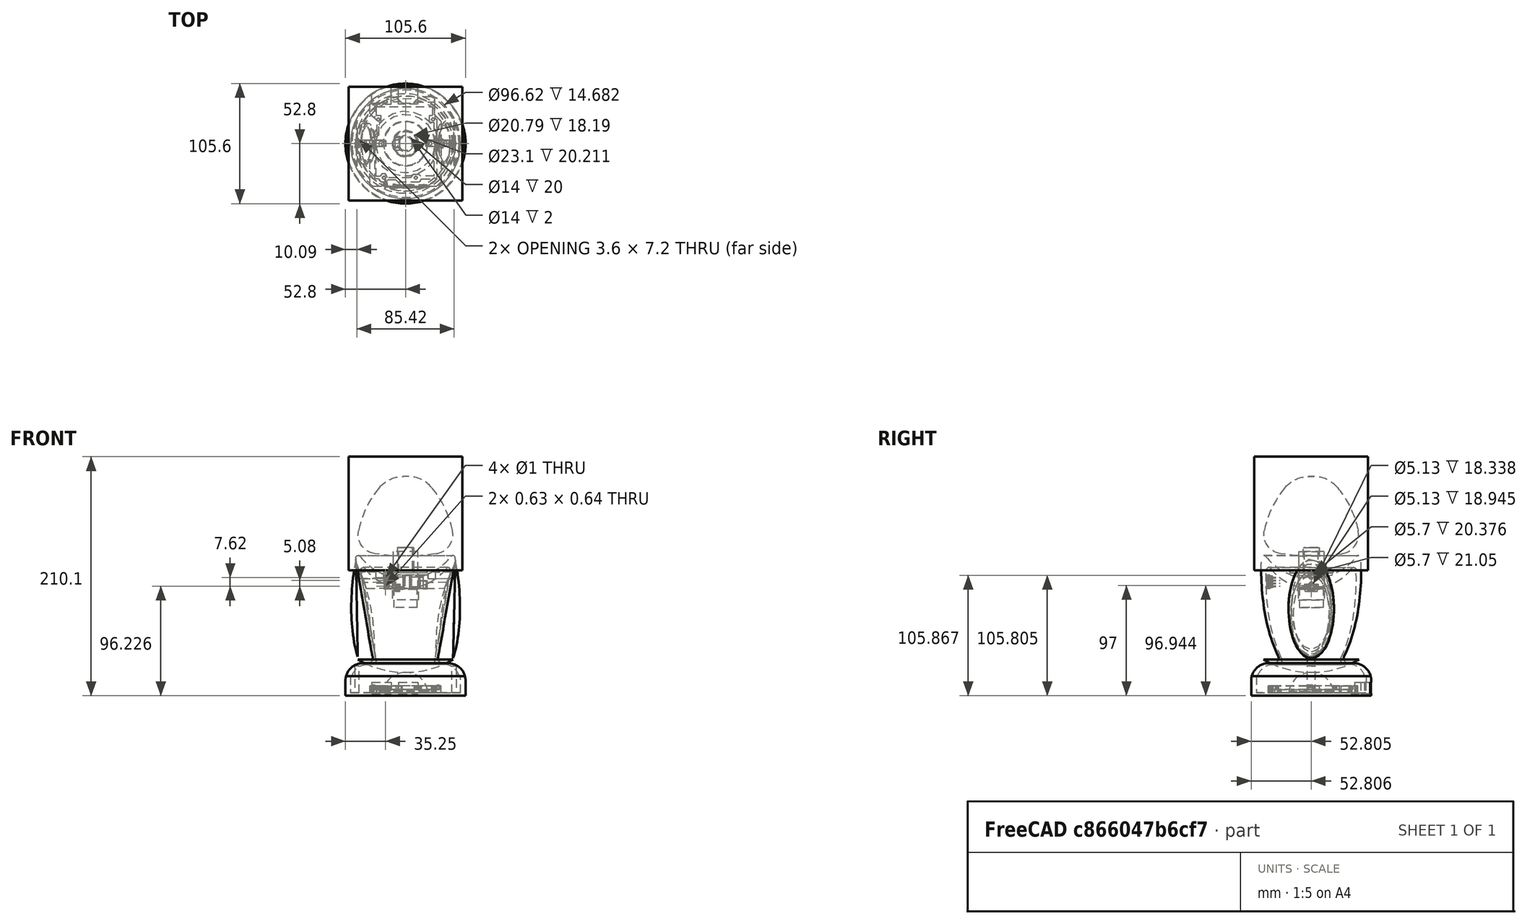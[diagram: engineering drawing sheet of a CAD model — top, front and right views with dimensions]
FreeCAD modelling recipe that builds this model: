
FCSTD DOCUMENT  (FreeCAD 0.20R29410 (Git))
Label: evaV1
License: All rights reserved
LicenseURL: https://en.wikipedia.org/wiki/All_rights_reserved
objects: Part::FeaturePython×33, Part::Cut×16, App::DocumentObjectGroup×11, Part::Part2DObjectPython×11, Part::Feature×9, Part::MultiFuse×9, Part::Extrusion×8, Part::Box×8, Raytracing::LuxFeature×8, Part::Sphere×4, Part::Cylinder×4, Part::Fillet×3, App::FeaturePython×3, Mesh::Feature×2, Sketcher::SketchObject×1, Part::Revolution×1, Part::Refine×1, Raytracing::LuxProject×1
note: 108 computed .brp shape members not serialized (recipe doc carries the construction recipe); baked Part::Feature solids carry a one-line shape summary decoded from their .brp

FEATURE [Part::Sphere] Sphere
  Angle1 = -90
  Angle2 = 10
  Angle3 = 360
  AttacherType = Attacher::AttachEngine3D
  Placement = pos=(0,0,0.478785) rot=(0,0,1;0rad)
  Radius = 20
FEATURE [Part::FeaturePython] Clone  label="Sphere001"  # Draft clone (typed FeaturePython)
  AttacherType = Attacher::AttachEngine3D
  Fuse = false
  Objects = -> [Sphere]
  Placement = pos=(0,0,-4.51485) rot=(0,0,1;0rad)
  Scale = (1,1,2.3)
FEATURE [Part::Sphere] Sphere001  label="Sphere002"
  Angle1 = -90
  Angle2 = 90
  Angle3 = 360
  AttacherType = Attacher::AttachEngine3D
  Placement = pos=(0,0,14.8901) rot=(0,0,1;0rad)
  Radius = 23
FEATURE [Part::Cut] Cut  label="Body"
  Base = -> Clone
  Tool = -> Sphere001
FEATURE [Part::Fillet] Fillet  label="EvaBody"
  Base = -> Cut
  Edges = 1 edges r=1: [Edge1]
  Placement = pos=(0,0,54.9218) rot=(0,0,1;0rad)
FEATURE [Part::Sphere] Sphere003  label="Sphere004"
  Angle1 = -90
  Angle2 = -60
  Angle3 = 360
  AttacherType = Attacher::AttachEngine3D
  Placement = pos=(-0.0204827,0,65.9269) rot=(0,0,1;0rad)
  Radius = 39.5
FEATURE [Part::FeaturePython] Clone002  label="Sphere005"  # Draft clone (typed FeaturePython)
  AttacherType = Attacher::AttachEngine3D
  Fuse = false
  Objects = -> [Sphere003]
  Placement = pos=(-0.0204827,1e-15,104.24) rot=(0,0,1;0rad)
  Scale = (2.12,2.12,2.12)
FEATURE [Part::Sphere] Sphere002  label="UpperHead"
  Angle1 = 10
  Angle2 = 90
  Angle3 = 360
  AttacherType = Attacher::AttachEngine3D
  Placement = pos=(0,0,0.478785) rot=(0,0,1;0rad)
  Radius = 20
FEATURE [App::DocumentObjectGroup] Group  label="Build"
  Group = -> [Sphere003,Clone002,Sphere002]
FEATURE [Sketcher::SketchObject] Sketch  label="HeadSketch"
  FullyConstrained = false
  MapMode = 2
  Placement = pos=(0,0,54.9218) rot=(0,0,1;0rad)
  Support = -> [Fillet]
  sketch-geometry (24):
    g0: LineSegment StartX=-21.7965 StartY=-11.3382 StartZ=0 EndX=21.2048 EndY=-12.4097 EndZ=0
    g1: Circle CenterX=0 CenterY=0 CenterZ=0 NormalX=0 NormalY=0 NormalZ=1 AngleXU=0 Radius=24.5691
    g2: LineSegment StartX=21.3552 StartY=0 StartZ=0 EndX=13.3962 EndY=-0.101077 EndZ=0
    g3: LineSegment StartX=-13.3802 StartY=-0.143385 StartZ=0 EndX=-19.9121 EndY=0 EndZ=0
    g4: LineSegment StartX=-3.37523e-05 StartY=-11.8813 StartZ=0 EndX=0 EndY=-22.0143 EndZ=0
    g5: LineSegment StartX=13.3962 StartY=-0.101077 StartZ=0 EndX=-3.37523e-05 EndY=-11.8813 EndZ=0
    g6: LineSegment StartX=-13.3802 StartY=-0.143385 StartZ=0 EndX=-3.37523e-05 EndY=-11.8813 EndZ=0
    g7: LineSegment StartX=0 StartY=17.1433 StartZ=0 EndX=0.581079 EndY=17.1433 EndZ=0
    g8: LineSegment StartX=20.5247 StartY=13.5047 StartZ=0 EndX=23.5963 EndY=12.9178 EndZ=0
    g9: GeomPoint X=0 Y=-1.93536 Z=0
    g10: LineSegment StartX=7.19648 StartY=-0.989266 StartZ=0 EndX=0 EndY=-1.93536 EndZ=0
    g11: LineSegment StartX=0 StartY=-1.93536 StartZ=0 EndX=-7.03873 EndY=-0.87588 EndZ=0
    g12: LineSegment StartX=0 StartY=17.1433 StartZ=0 EndX=0 EndY=0 EndZ=0
    g13: ArcOfCircle CenterX=0.581079 CenterY=9.86833 CenterZ=0 NormalX=0 NormalY=0 NormalZ=1 AngleXU=0 Radius=7.27493 StartAngle=0.693262 EndAngle=1.5708
    g14: ArcOfCircle CenterX=-0.581079 CenterY=9.88205 CenterZ=0 NormalX=0 NormalY=0 NormalZ=1 AngleXU=0 Radius=7.26121 StartAngle=1.5708 EndAngle=2.33078
    g15: LineSegment StartX=6.74134 StartY=12.7057 StartZ=0 EndX=0.581079 EndY=17.1433 EndZ=0
    g16: LineSegment StartX=-6.7178 StartY=12.6732 StartZ=0 EndX=-0.581079 EndY=17.1433 EndZ=0
    g17: ArcOfCircle CenterX=6.60715 CenterY=3.49348 CenterZ=0 NormalX=0 NormalY=0 NormalZ=1 AngleXU=0 Radius=4.52132 StartAngle=4.84311 EndAngle=6.48567
    g18: ArcOfCircle CenterX=-6.35756 CenterY=3.64951 CenterZ=0 NormalX=0 NormalY=0 NormalZ=1 AngleXU=0 Radius=4.57636 StartAngle=3.05715 EndAngle=4.56299
    g19: LineSegment StartX=10.3085 StartY=5.26228 StartZ=0 EndX=7.19648 EndY=-0.989266 EndZ=0
    g20: LineSegment StartX=-7.03873 StartY=-0.87588 StartZ=0 EndX=-10.097 EndY=5.40212 EndZ=0
    g21: ArcOfCircle CenterX=-11.5876 CenterY=-0.241793 CenterZ=0 NormalX=0 NormalY=0 NormalZ=1 AngleXU=0 Radius=23.0955 StartAngle=0.202481 EndAngle=0.693262
    g22: ArcOfCircle CenterX=6.36602 CenterY=2.57249 CenterZ=0 NormalX=0 NormalY=0 NormalZ=1 AngleXU=0 Radius=17.3454 StartAngle=2.33078 EndAngle=3.05715
    g23: LineSegment StartX=0 StartY=-1.93536 StartZ=0 EndX=0 EndY=17.1433 EndZ=0
  constraints (30):
    c: PointOnObject(g0,g1)
    c: PointOnObject(g0,g1)
    c: Coincident(g1,g-1)
    c: PointOnObject(g2,g-1)
    c: PointOnObject(g4,g0)
    c: Coincident(g5,g2)
    c: Coincident(g5,g4)
    c: Coincident(g6,g3)
    c: Coincident(g6,g5)
    c: Horizontal(g7)
    c: PointOnObject(g8,g1)
    c: PointOnObject(g9,g-2)
    c: Coincident(g10,g9)
    c: Coincident(g11,g10)
    c: Coincident(g12,g1)
    c: Tangent(g7,g13) = 1.5708
    c: Coincident(g15,g7)
    c: Equal(g15,g16)
    c: Vertical(g12)
    c: Tangent(g10,g17) = 1.5708
    c: Tangent(g11,g18) = 1.5708
    c: Coincident(g19,g10)
    c: Coincident(g20,g11)
    c: Equal(g19,g20)
    c: Tangent(g17,g21) = -1.5708
    c: Tangent(g13,g21) = -1.5708
    c: Tangent(g14,g22) = -1.5708
    c: Tangent(g18,g22) = -1.5708
    c: Coincident(g23,g10)
    c: PointOnObject(g7,g12)
FEATURE [Part::Feature] Sketch001
  shape: bbox 11.13 x 19.08 x 2e-07 mm, 0 faces, 0 solids (baked)
FEATURE [Part::Revolution] Revolve
  Angle = 360
  Axis = (0,1,0)
  Base = (0,0,0)
  FaceMakerClass = Part::FaceMakerBullseye
  Placement = pos=(0,-1.30463,1.78342) rot=(1,0,0;1.5708rad)
  Solid = false
  Source = -> Sketch001
  Symmetric = false
FEATURE [Part::FeaturePython] Clone003  label="Head"  # Draft clone (typed FeaturePython)
  AttacherType = Attacher::AttachEngine3D
  Fuse = false
  Objects = -> [Revolve]
  Placement = pos=(0,2.70425e-10,58.4524) rot=(1,0,0;1.5708rad)
  Scale = (1.7,1.7,1.7)
FEATURE [Part::Cylinder] Cylinder  label="Neck"
  Angle = 360
  AttacherType = Attacher::AttachEngine3D
  FirstAngle = 0
  Height = 15
  Placement = pos=(0,0,42.6404) rot=(0,0,1;0rad)
  Radius = 5
  SecondAngle = 0
FEATURE [Part::Cylinder] Cylinder001  label="Base"
  Angle = 360
  AttacherType = Attacher::AttachEngine3D
  FirstAngle = 0
  Height = 13
  Radius = 24
  SecondAngle = 0
FEATURE [App::DocumentObjectGroup] Group002  label="Drafts"
  Group = -> [Sphere,Group,Sketch,Revolve]
FEATURE [Part::Part2DObjectPython] Rectangle  label="ArmCut"  # Draft 2D object (typed FeaturePython)
  Area = 5447.74
  ChamferSize = 0
  Columns = 1
  FilletRadius = 0
  Height = 81.8196
  Length = 66.5823
  MakeFace = true
  Placement = pos=(-12.9997,-33.2912,14.176) rot=(0.541699,0.541699,0.642747;1.99907rad)
  Rows = 1
FEATURE [Part::Part2DObjectPython] Clone2D  label="ArmCutLeft"  # Draft 2D object (typed FeaturePython)
  Fuse = false
  Objects = -> [Rectangle]
  Placement = pos=(12.8819,-33.2912,14.5327) rot=(0.608338,0.608338,0.509755;2.19875rad)
  Scale = (1,1,1)
FEATURE [Part::FeaturePython] Slice  # WARN: FeaturePython — macro-defined, semantics opaque (R4)
  Base = -> Fillet
  Mode = 1
  Tolerance = 0
  Tools = -> [Clone2D,Rectangle]
FEATURE [Part::FeaturePython] Slice_child0  label="Slice.0"  # WARN: FeaturePython — macro-defined, semantics opaque (R4)
  Base = -> Slice
  FilterType = 1
  Invert = false
  OverrideMaxVal = 0
  WindowFrom = 80
  WindowTo = 100
  items = 0
FEATURE [Part::FeaturePython] Slice_child1  label="RightArm"  # WARN: FeaturePython — macro-defined, semantics opaque (R4)
  Base = -> Slice
  FilterType = 1
  Invert = false
  OverrideMaxVal = 0
  Placement = pos=(8.47277,0,-2.40038) rot=(0,-1,0;0.152637rad)
  WindowFrom = 80
  WindowTo = 100
  items = 1
FEATURE [Part::FeaturePython] Slice_child2  label="LeftArm"  # WARN: FeaturePython — macro-defined, semantics opaque (R4)
  Base = -> Slice
  FilterType = 1
  Invert = false
  OverrideMaxVal = 0
  Placement = pos=(-8.37005,0,-2.38162) rot=(0,1,0;0.152455rad)
  WindowFrom = 80
  WindowTo = 100
  items = 2
FEATURE [Part::FeaturePython] Clone004  label="Slice.003"  # Draft clone (typed FeaturePython)
  AttacherType = Attacher::AttachEngine3D
  Fuse = false
  Objects = -> [Slice_child2]
  Placement = pos=(-33.7337,0,70.5771) rot=(0,1,0;3.14159rad)
  Scale = (1,1,1)
FEATURE [Part::FeaturePython] Clone005  label="Slice.004"  # Draft clone (typed FeaturePython)
  AttacherType = Attacher::AttachEngine3D
  Fuse = false
  Objects = -> [Slice_child1]
  Placement = pos=(33.43,0,69.7879) rot=(0,1,0;3.14159rad)
  Scale = (1,1,1)
FEATURE [Part::Cut] Cut001
  Base = -> Slice_child0
  Tool = -> Clone004
FEATURE [Part::Cut] Cut002  label="CuttedBody"
  Base = -> Cut001
  Tool = -> Clone005
FEATURE [Part::Part2DObjectPython] Circle  # Draft 2D object (typed FeaturePython)
  Area = 4.35646
  FirstAngle = 0
  LastAngle = 0
  MakeFace = true
  Placement = pos=(-19.6772,0.00266592,48.0107) rot=(0,1,0;1.55304rad)
  Radius = 1.17758
FEATURE [Part::Extrusion] Extrude002  label="RightArm Support"
  Base = -> Circle
  Dir = (0.999842,2e-15,0.0177575)
  DirMode = 2
  FaceMakerClass = Part::FaceMakerBullseye
  LengthFwd = 8
  LengthRev = 0
  Placement = pos=(31.7394,1.9e-15,0) rot=(0,0,1;0rad)
  Solid = false
  Symmetric = false
FEATURE [Part::FeaturePython] Clone006  label="LeftArm Support001"  # Draft clone (typed FeaturePython)
  AttacherType = Attacher::AttachEngine3D
  Fuse = false
  Objects = -> [Extrude002]
  Placement = pos=(-0.14219,0,0) rot=(0,0,1;0rad)
  Scale = (1,1,1)
FEATURE [Part::Part2DObjectPython] Clone2D001  label="Circle (2D)"  # Draft 2D object (typed FeaturePython)
  Fuse = false
  Objects = -> [Circle]
  Placement = pos=(-19.6772,0.00266592,48.0107) rot=(0,1,0;1.55304rad)
  Scale = (1.1,1.1,1.1)
FEATURE [Part::Extrusion] Extrude003  label="ExtrusionHoleLeft"
  Base = -> Clone2D001
  Dir = (0.999842,2e-15,0.0177575)
  DirMode = 2
  FaceMakerClass = Part::FaceMakerBullseye
  LengthFwd = 11
  LengthRev = 0
  Placement = pos=(28.742,1.8e-15,0) rot=(0,0,1;0rad)
  Solid = false
  Symmetric = false
FEATURE [Part::FeaturePython] Clone007  label="ExtrusionHoleRight"  # Draft clone (typed FeaturePython)
  AttacherType = Attacher::AttachEngine3D
  Fuse = false
  Objects = -> [Extrude003]
  Scale = (1,1,1)
FEATURE [Part::Cut] Cut003
  Base = -> Cut002
  Tool = -> Extrude003
FEATURE [Part::Cut] Cut004  label="BodyWithArmHoles"
  Base = -> Cut003
  Tool = -> Clone007
FEATURE [Part::MultiFuse] Fusion  label="RightArmWithSupport"
  Shapes = -> [Slice_child1,Extrude002]
FEATURE [Part::Part2DObjectPython] Circle001  # Draft 2D object (typed FeaturePython)
  Area = 237.663
  FirstAngle = 0
  LastAngle = 0
  MakeFace = true
  Placement = pos=(1e-15,0,57.6404) rot=(0,0,1;0rad)
  Radius = 8.69772
FEATURE [Part::Extrusion] Extrude  label="NeckBlock"
  Base = -> Circle001
  Dir = (0,0,1)
  DirMode = 2
  FaceMakerClass = Part::FaceMakerBullseye
  LengthFwd = 1
  LengthRev = 0
  Placement = pos=(0,0,-8.59498) rot=(0,0,1;0rad)
  Solid = false
  Symmetric = false
FEATURE [Part::MultiFuse] Fusion001  label="LeftArmWithSupport"
  Shapes = -> [Slice_child2,Clone006]
FEATURE [Part::FeaturePython] Clone009  label="ExpandedNeck"  # Draft clone (typed FeaturePython)
  AttacherType = Attacher::AttachEngine3D
  Fuse = false
  Objects = -> [Cylinder]
  Placement = pos=(0,0,38.2322) rot=(0,0,1;0rad)
  Scale = (1.05,1.05,1.05)
FEATURE [Part::Cut] Cut005  label="BodyWithNeckHole"
  Base = -> Cut004
  Tool = -> Clone009
FEATURE [Part::MultiFuse] Fusion002  label="NeckWithBlock"
  Shapes = -> [Cylinder,Extrude]
FEATURE [Part::FeaturePython] Clone010  label="ExpandedNeck001"  # Draft clone (typed FeaturePython)
  AttacherType = Attacher::AttachEngine3D
  Fuse = false
  Objects = -> [Clone009]
  Placement = pos=(0,0,51.4204) rot=(0,0,1;0rad)
  Scale = (1,1,1)
FEATURE [Part::Cut] Cut006  label="HeadWithNeckHole"
  Base = -> Clone003
  Tool = -> Clone010
FEATURE [Part::MultiFuse] Fusion003  label="BodyWithBase"
  Shapes = -> [Cylinder001,Cut005]
FEATURE [Part::Fillet] Fillet001  label="RoundedBodyBase"
  Base = -> Fusion003
  Edges = 1 edges r=2: [Edge4]
FEATURE [Part::Fillet] Fillet002  label="RoundedBodyWithBase"
  Base = -> Fillet001
  Edges = 1 edges r=7: [Edge4]
FEATURE [App::DocumentObjectGroup] GrExplode_Slice  label="Non-Sized-Parts"
  Group = -> [Fusion,Fusion001,Fusion002,Cut006,Fillet002]
FEATURE [App::DocumentObjectGroup] Group003  label="Build001"
  Group = -> [Fusion003]
FEATURE [Mesh::Feature] Alhambra_II_Support_NO_text  label="Alhambra-II-Support-NO-text"
FEATURE [Part::Feature] Alhambra_II_Support_NO_text001
  shape: bbox 78.88 x 62.84 x 6.975 mm, 1078 faces, 0 solids (baked)
FEATURE [Part::Refine] Alhambra_II_Support_NO_text001001  label="RefinedFPGASupport"
  Placement = pos=(2.6e-14,86.6242,2.50937) rot=(0,0,-1;1.5708rad)
  Source = -> Alhambra_II_Support_NO_text001
FEATURE [Part::FeaturePython] Clone011  label="RightArmWithSupport001"  # Draft clone (typed FeaturePython)
  AttacherType = Attacher::AttachEngine3D
  Fuse = false
  Objects = -> [Fusion]
  Scale = (2.2,2.2,2.2)
FEATURE [Part::FeaturePython] Clone012  label="LeftArmWithSupport001"  # Draft clone (typed FeaturePython)
  AttacherType = Attacher::AttachEngine3D
  Fuse = false
  Objects = -> [Fusion001]
  Scale = (2.2,2.2,2.2)
FEATURE [Part::FeaturePython] Clone013  label="NeckWithBlock001"  # Draft clone (typed FeaturePython)
  AttacherType = Attacher::AttachEngine3D
  Fuse = false
  Objects = -> [Fusion002]
  Scale = (2.2,2.2,2.2)
FEATURE [Part::FeaturePython] Clone014  label="HeadWithNeckHole001"  # Draft clone (typed FeaturePython)
  AttacherType = Attacher::AttachEngine3D
  Fuse = false
  Objects = -> [Cut006]
  Scale = (2.2,2.2,2.2)
FEATURE [Part::FeaturePython] Clone015  label="RoundedBodyWithBase001"  # Draft clone (typed FeaturePython)
  AttacherType = Attacher::AttachEngine3D
  Fuse = false
  Objects = -> [Fillet002]
  Scale = (2.2,2.2,2.2)
FEATURE [App::DocumentObjectGroup] Group005  label="Resized Parts"
  Group = -> [Clone011,Clone012,Clone013,Clone014,Clone015]
FEATURE [Part::Part2DObjectPython] Rectangle001  label="BaseSlicer"  # Draft 2D object (typed FeaturePython)
  Area = 17833.6
  ChamferSize = 0
  Columns = 1
  FilletRadius = 0
  Height = 133.871
  Length = 133.215
  MakeFace = true
  Placement = pos=(-69.7967,-69.2809,17.1918) rot=(0,0,1;0rad)
  Rows = 1
FEATURE [Part::FeaturePython] Slice001  label="BodySlice"  # WARN: FeaturePython — macro-defined, semantics opaque (R4)
  Base = -> Clone015
  Mode = 1
  Tolerance = 0
  Tools = -> [Rectangle001]
FEATURE [Part::FeaturePython] Slice001_child0  label="EvaBody001"  # WARN: FeaturePython — macro-defined, semantics opaque (R4)
  Base = -> Slice001
  FilterType = 1
  Invert = false
  OverrideMaxVal = 0
  WindowFrom = 80
  WindowTo = 100
  items = 0
FEATURE [Part::FeaturePython] Slice001_child1  label="FPGABase"  # WARN: FeaturePython — macro-defined, semantics opaque (R4)
  Base = -> Slice001
  FilterType = 1
  Invert = false
  OverrideMaxVal = 0
  WindowFrom = 80
  WindowTo = 100
  items = 1
FEATURE [Part::Part2DObjectPython] Circle002  # Draft 2D object (typed FeaturePython)
  Area = 7332.14
  FirstAngle = 0
  LastAngle = 0
  MakeFace = true
  Placement = pos=(-7.1e-15,-3.9e-15,17.1918) rot=(0,0,1;0rad)
  Radius = 48.3104
FEATURE [Part::Extrusion] Extrude005
  Base = -> Circle002
  Dir = (0,0,1)
  DirMode = 2
  FaceMakerClass = Part::FaceMakerBullseye
  LengthFwd = 15
  LengthRev = 0
  Placement = pos=(0,0,-14.6824) rot=(0,0,1;0rad)
  Solid = false
  Symmetric = false
FEATURE [Part::Cut] Cut007  label="HollowFPGABase"
  Base = -> Slice001_child1
  Tool = -> Extrude005
FEATURE [Part::Box] Box  label="Cubo"
  AttacherType = Attacher::AttachEngine3D
  Height = 10
  Length = 17
  Placement = pos=(-6.05737,34.8465,1.87069) rot=(0,0,1;0rad)
  Width = 30
FEATURE [Part::Cut] Cut008  label="FPGABaseWConnectionHole1"
  Base = -> Cut007
  Tool = -> Box
FEATURE [Part::FeaturePython] Clone016  label="Cubo001"  # Draft clone (typed FeaturePython)
  AttacherType = Attacher::AttachEngine3D
  Fuse = false
  Objects = -> [Box]
  Placement = pos=(-29.6318,34.8465,1.87069) rot=(0,0,1;0rad)
  Scale = (1,1,1)
FEATURE [Part::Cut] Cut009  label="FPGABaseWithHoles"
  Base = -> Cut008
  Tool = -> Clone016
FEATURE [Part::FeaturePython] Clone018  label="EvaBodyHollow001"  # WARN: FeaturePython — macro-defined, semantics opaque (R4)
  AttacherType = Attacher::AttachEngine3D
  Fuse = false
  Placement = pos=(-1e-15,0,1.71918) rot=(0,0,1;0rad)
  Scale = (0.9,0.9,0.9)
FEATURE [Part::Feature] Shell_solid  label="EvaBodyHollow"
  shape: bbox 204.6 x 181.6 x 135.9 mm, 34 faces (baked)
FEATURE [Part::Cylinder] Cylinder002  label="LeftBridge"
  Angle = 180
  AttacherType = Attacher::AttachEngine3D
  FirstAngle = 0
  Height = 26
  Placement = pos=(-40.91,0,0) rot=(0,0,1;1.5708rad)
  Radius = 3.6
  SecondAngle = 0
FEATURE [Part::Cylinder] Cylinder003  label="RightBridge"
  Angle = 180
  AttacherType = Attacher::AttachEngine3D
  FirstAngle = 0
  Height = 26
  Placement = pos=(40.91,0,0) rot=(0,0,-1;1.5708rad)
  Radius = 3.6
  SecondAngle = 0
FEATURE [Part::FeaturePython] Clone019  label="LeftBridge001"  # Draft clone (typed FeaturePython)
  AttacherType = Attacher::AttachEngine3D
  Fuse = false
  Objects = -> [Cylinder002]
  Placement = pos=(-40.91,0,0) rot=(0,0,1;1.5708rad)
  Scale = (1,1,1)
FEATURE [Part::FeaturePython] Clone020  label="RightBridge001"  # Draft clone (typed FeaturePython)
  AttacherType = Attacher::AttachEngine3D
  Fuse = false
  Objects = -> [Cylinder003]
  Placement = pos=(40.91,0,0) rot=(0,0,-1;1.5708rad)
  Scale = (1,1,1)
FEATURE [Part::Cut] Cut010  label="EvaConnectableLeft"
  Base = -> Shell_solid
  Tool = -> Clone019
FEATURE [Part::Cut] Cut011  label="EvaBodyConnectable"
  Base = -> Cut010
  Tool = -> Clone020
FEATURE [Part::MultiFuse] Fusion004  label="BaseFPGAWithBridges"
  Shapes = -> [Cylinder003,Cylinder002,Cut009]
FEATURE [Mesh::Feature] Servo_SG90  label="Servo-SG90"
FEATURE [App::DocumentObjectGroup] Group004  label="External"
  Group = -> [Alhambra_II_Support_NO_text001001,Servo_SG90,Alhambra_II_Support_NO_text001,Alhambra_II_Support_NO_text]
FEATURE [Part::Feature] Servo_SG90001  label="RefinedServo"
  Placement = pos=(16.3519,-0.186281,64.3614) rot=(0,0,1;1.5708rad)
  shape: bbox 32.4 x 11.8 x 29.9 mm, 2326 faces, 0 solids (baked)
FEATURE [App::FeaturePython] Dimension  # Draft dimension (typed FeaturePython)
  Diameter = false
  Dimline = (-23.6882,-74.8393,0)
  Direction = (0,0,0)
  Distance = 105.6
  End = (52.8,-1.32e-14,0)
  Normal = (0,0,-1)
  Start = (-52.8,2.99e-14,0)
FEATURE [App::FeaturePython] Dimension001  # Draft dimension (typed FeaturePython)
  Diameter = false
  Dimline = (-91.8745,5.94944e-10,192.711)
  Direction = (0,0,0)
  Distance = 192.711
  End = (0,5.94949e-10,192.711)
  Normal = (0,0,1)
  Start = (-1.8e-15,-2.1e-15,0)
FEATURE [App::FeaturePython] Dimension002  # Draft dimension (typed FeaturePython)
  Diameter = false
  Dimline = (-43.7741,108.073,121.137)
  Direction = (0,0,0)
  Distance = 87.5482
  End = (-43.7741,205.609,121.137)
  Normal = (0,0,1)
  Start = (43.7741,205.609,121.137)
FEATURE [Part::Feature] Feature  label="OLED_0.91_128x034"
  Placement = pos=(0,-36.5535,100.036) rot=(1,0,0;1.5708rad)
  shape: bbox 38.3 x 11.46 x 12.1 mm, 1137 faces, 52 solids (baked)
FEATURE [Part::Feature] Alhambra_II_Support_NO_text001001_solid  label="RefinedFPGASupport (Solid)"
  shape: bbox 62.84 x 78.88 x 6.975 mm, 342 faces (baked)
FEATURE [Part::MultiFuse] Fusion005  label="BaseFPGA"
  Shapes = -> [Alhambra_II_Support_NO_text001001_solid,Fusion004]
FEATURE [App::DocumentObjectGroup] Group008  label="Measurements"
  Group = -> [Dimension,Dimension001,Dimension002]
FEATURE [Part::FeaturePython] Clone021  label="RightArmWithSupport002"  # Draft clone (typed FeaturePython)
  AttacherType = Attacher::AttachEngine3D
  Fuse = false
  Objects = -> [Clone011]
  Scale = (1,1,1)
FEATURE [Part::FeaturePython] Clone022  label="LeftArmWithSupport002"  # Draft clone (typed FeaturePython)
  AttacherType = Attacher::AttachEngine3D
  Fuse = false
  Objects = -> [Clone012]
  Scale = (1,1,1)
FEATURE [Part::FeaturePython] Clone023  label="NeckWithBlock002"  # Draft clone (typed FeaturePython)
  AttacherType = Attacher::AttachEngine3D
  Fuse = false
  Objects = -> [Clone013]
  Scale = (1,1,1)
FEATURE [Part::Feature] Clone023_solid  label="NeckWithBlock002 (Solid)"
  shape: bbox 38.27 x 38.27 x 33 mm, 7 faces (baked)
FEATURE [Part::FeaturePython] Clone024  label="HeadWithNeckHole002"  # Draft clone (typed FeaturePython)
  AttacherType = Attacher::AttachEngine3D
  Fuse = false
  Objects = -> [Clone014]
  Scale = (1,1,1)
FEATURE [Part::Box] Box001  label="BridgeHole1"
  AttacherType = Attacher::AttachEngine3D
  Height = 5.3
  Length = 5
  Placement = pos=(-9.5,-6,92.81) rot=(0,0,1;0rad)
  Width = 3
FEATURE [Part::Box] Box002  label="Cubo003"
  AttacherType = Attacher::AttachEngine3D
  Height = 1
  Length = 4
  Placement = pos=(0,1,0) rot=(0,0,1;0rad)
  Width = 7
FEATURE [Part::Box] Box003  label="Cubo004"
  AttacherType = Attacher::AttachEngine3D
  Height = 5.3
  Length = 4
  Placement = pos=(0,-1,0) rot=(0,0,1;0rad)
  Width = 2
FEATURE [Part::Box] Box006  label="Cubo005"
  AttacherType = Attacher::AttachEngine3D
  Height = 100
  Length = 100
  Placement = pos=(-50,-50,110.1) rot=(0,0,1;0rad)
  Width = 100
FEATURE [Part::Box] Box007  label="Cubo006"
  AttacherType = Attacher::AttachEngine3D
  Height = 5.3
  Length = 4
  Placement = pos=(0,8,0) rot=(0,0,1;0rad)
  Width = 2
FEATURE [Part::Box] Box008  label="BridgeHole2"
  AttacherType = Attacher::AttachEngine3D
  Height = 5.3
  Length = 5
  Placement = pos=(-9.5,3,92.81) rot=(0,0,1;0rad)
  Width = 3
FEATURE [Part::MultiFuse] Fusion007  label="Bridge"
  Placement = pos=(-9,-4.5,91.81) rot=(0,0,1;0rad)
  Shapes = -> [Box003,Box002,Box007]
FEATURE [Part::Feature] Solid001
  shape: bbox 22 x 22 x 1.001 mm, 13 faces (baked)
FEATURE [App::DocumentObjectGroup] Group009  label="Tests"
  Group = -> [Solid001,Box006]
FEATURE [Part::Feature] Solid  label="Head001"
  shape: bbox 90.1 x 90.1 x 69.84 mm, 6 faces (baked)
FEATURE [Part::MultiFuse] Fusion008  label="HeadWithNeck"
  Shapes = -> [Clone023_solid,Solid]
FEATURE [App::DocumentObjectGroup] Group006  label="Building"
  Group = -> [Slice001_child0,Clone018,Clone024,Clone023,Fusion008]
FEATURE [Part::FeaturePython] Clone025  label="HeadWithNeck001"  # Draft clone (typed FeaturePython)
  AttacherType = Attacher::AttachEngine3D
  Fuse = false
  Objects = -> [Fusion008]
  Scale = (1,1,1)
FEATURE [Part::Box] Box009  label="Cubo007"
  AttacherType = Attacher::AttachEngine3D
  Height = 100
  Length = 100
  Placement = pos=(-50,-50,110.1) rot=(0,0,1;0rad)
  Width = 100
FEATURE [Part::FeaturePython] Slice002  # WARN: FeaturePython — macro-defined, semantics opaque (R4)
  Base = -> Clone025
  Mode = 1
  Tolerance = 0
  Tools = -> [Box009]
FEATURE [Part::FeaturePython] Slice002_child0  label="LowerHead001"  # WARN: FeaturePython — macro-defined, semantics opaque (R4)
  Base = -> Slice002
  FilterType = 1
  Invert = false
  OverrideMaxVal = 0
  WindowFrom = 80
  WindowTo = 100
  items = 0
FEATURE [Part::FeaturePython] Slice002_child1  label="LowerHead"  # WARN: FeaturePython — macro-defined, semantics opaque (R4)
  Base = -> Slice002
  FilterType = 1
  Invert = false
  OverrideMaxVal = 0
  WindowFrom = 80
  WindowTo = 100
  items = 1
FEATURE [Part::Part2DObjectPython] Circle003  # Draft 2D object (typed FeaturePython)
  Area = 153.938
  FirstAngle = 0
  LastAngle = 0
  MakeFace = true
  Placement = pos=(-2e-15,0,110.1) rot=(0.707107,-0.707107,0;3.14159rad)
  Radius = 7
FEATURE [Part::Part2DObjectPython] Circle004  # Draft 2D object (typed FeaturePython)
  Area = 113.097
  FirstAngle = 0
  LastAngle = 0
  MakeFace = true
  Placement = pos=(-2e-15,0,110.1) rot=(0.707107,-0.707107,0;3.14159rad)
  Radius = 6
FEATURE [Part::Extrusion] Extrude006
  Base = -> Circle003
  Dir = (0,0,-1)
  DirMode = 2
  FaceMakerClass = Part::FaceMakerBullseye
  LengthFwd = -20
  LengthRev = 0
  Solid = false
  Symmetric = false
FEATURE [Part::Cut] Cut012  label="UpperHeadWithHole"
  Base = -> Slice002_child1
  Tool = -> Extrude006
FEATURE [Part::Extrusion] Extrude007
  Base = -> Circle004
  Dir = (0,0,-1)
  DirMode = 2
  FaceMakerClass = Part::FaceMakerBullseye
  LengthFwd = 30
  LengthRev = 0
  Placement = pos=(0,0,20) rot=(0,0,1;0rad)
  Solid = false
  Symmetric = false
FEATURE [App::DocumentObjectGroup] Group010  label="Grupo"
FEATURE [Part::MultiFuse] Fusion009  label="LowerHead002"
  Shapes = -> [Slice002_child0,Extrude007]
FEATURE [Part::Cut] Cut013
  Base = -> Fusion009
  Tool = -> Box008
FEATURE [Part::Cut] Cut014  label="BottomHeadWithHoles"
  Base = -> Cut013
  Tool = -> Box001
FEATURE [Raytracing::LuxFeature] Fusion005_View
  Result = <blob: 148354 chars omitted>
  Source = -> Fusion005
  Transparency = 0
FEATURE [Raytracing::LuxFeature] Servo_SG90001_View
  Result = <blob: 378046 chars omitted>
  Source = -> Servo_SG90001
  Transparency = 0
FEATURE [Raytracing::LuxFeature] Cut011_View
  Result = <blob: 1339024 chars omitted>
  Source = -> Cut011
  Transparency = 70
FEATURE [Raytracing::LuxFeature] Feature_View
  Result = <blob: 648450 chars omitted>
  Source = -> Feature
  Transparency = 0
FEATURE [Raytracing::LuxFeature] Clone022_View
  Result = <blob: 41529 chars omitted>
  Source = -> Clone022
  Transparency = 0
FEATURE [Raytracing::LuxFeature] Clone021_View
  Result = <blob: 39862 chars omitted>
  Source = -> Clone021
  Transparency = 0
FEATURE [Raytracing::LuxFeature] Clone023_View
  Result = <blob: 21989 chars omitted>
  Source = -> Clone023
  Transparency = 0
FEATURE [Raytracing::LuxFeature] Clone024_View
  Result = <blob: 236496 chars omitted>
  Source = -> Clone024
  Transparency = 0
FEATURE [Raytracing::LuxProject] LuxProject  label="LuxProjectRender"
  Camera = # declares position and view direction\n# Generated by FreeCAD (http://www.freecadweb.org/)\nLookAt 358.448 -280.888 420.043 61.9218 39.9128 158.342 -0.45207 0.274483 0.8487
  Group = -> [Fusion005_View,Servo_SG90001_View,Cut011_View,Feature_View,Clone022_View,Clone021_View,Clone023_View,Clone024_View]
  Template = A:/Program Files/FreeCAD 0.20/data/Mod/Raytracing/Templates/LuxOutdoor.lxs
FEATURE [Part::Part2DObjectPython] Circle005  # Draft 2D object (typed FeaturePython)
  Area = 153.938
  FirstAngle = 0
  LastAngle = 0
  MakeFace = true
  Placement = pos=(-1e-15,-1e-15,130.1) rot=(0,0,1;0rad)
  Radius = 7
FEATURE [Part::Extrusion] Extrude008
  Base = -> Circle005
  Dir = (0,0,1)
  DirMode = 2
  FaceMakerClass = Part::FaceMakerBullseye
  LengthFwd = -22
  LengthRev = 0
  Solid = false
  Symmetric = false
FEATURE [Part::Cut] Cut015  label="BottomNeck"
  Base = -> Cut014
  Tool = -> Extrude008
FEATURE [Part::Part2DObjectPython] Circle006  # Draft 2D object (typed FeaturePython)
  Area = 113.097
  FirstAngle = 0
  LastAngle = 0
  MakeFace = true
  Placement = pos=(-1e-15,-1e-15,130.1) rot=(0,0,1;0rad)
  Radius = 6
FEATURE [Part::Extrusion] Extrude009  label="Neck001"
  Base = -> Circle006
  Dir = (0,0,1)
  DirMode = 2
  FaceMakerClass = Part::FaceMakerBullseye
  LengthFwd = -22
  LengthRev = 0
  Solid = false
  Symmetric = false
FEATURE [App::DocumentObjectGroup] Group007  label="Eva"
  Group = -> [Fusion005,Servo_SG90001,Cut011,Feature,Clone022,Clone021,Fusion007,Cut012,Cut015,Extrude009]
